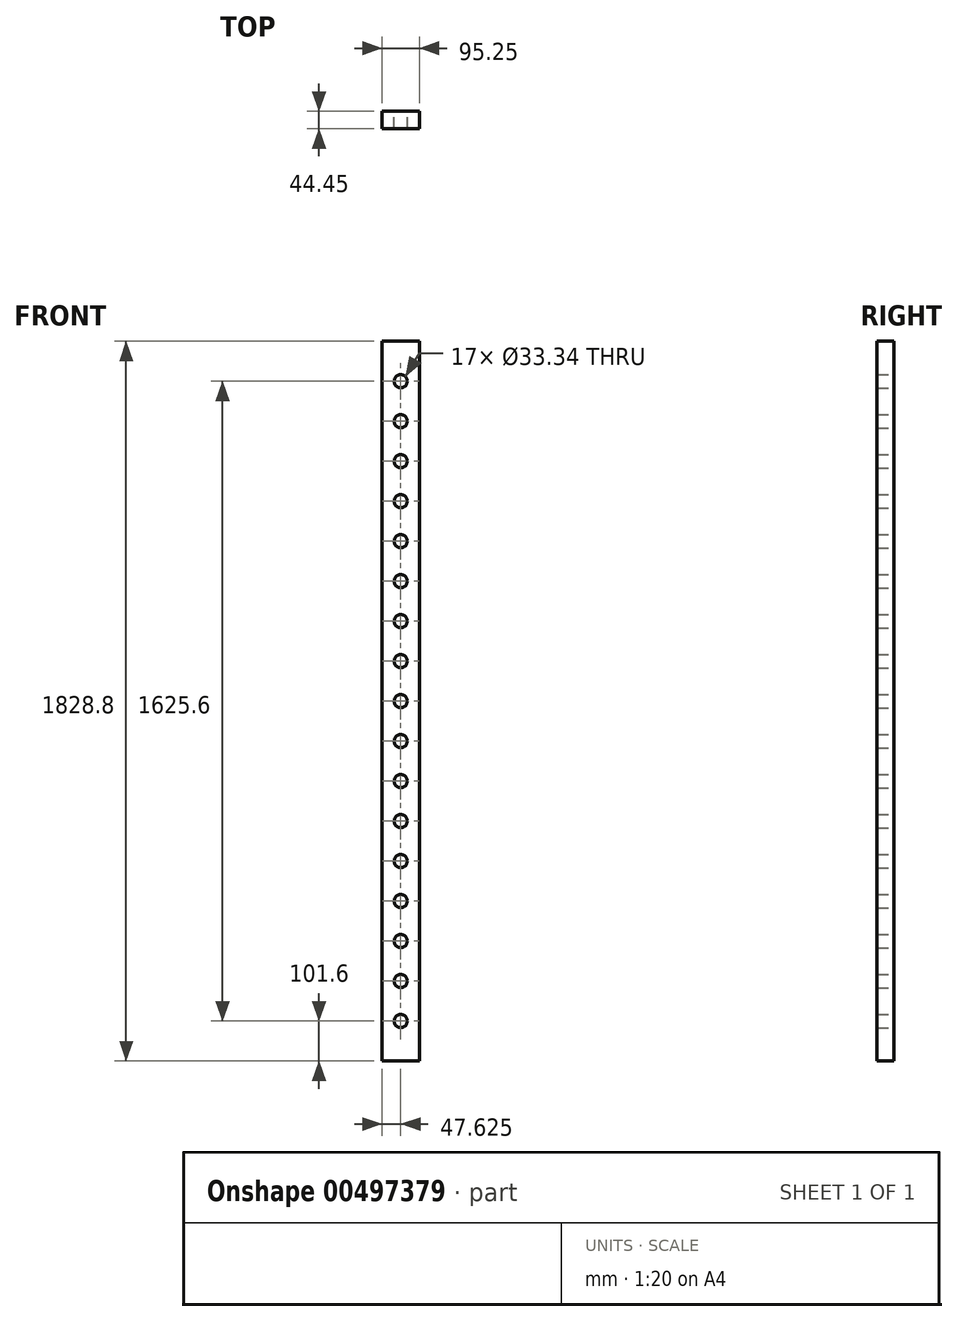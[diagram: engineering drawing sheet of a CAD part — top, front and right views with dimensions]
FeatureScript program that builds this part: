
annotation { "Feature Type Name" : "Feature", "Feature Type Description" : "" }
export const myFeature = defineFeature(function(context is Context, id is Id, definition is map)
    precondition{}
    {
        {
            var Q0;
            Q0=qCreatedBy(makeId("Front.planeOp"),FACE);
            var sketch = newSketch(context, id + "F0", { "sketchPlane" : qUnion([Q0])});
            skLineSegment(sketch, "E0.bottom", {"start": v(0, 0) * mm, "end": v(95.25, 0) * mm});
            skLineSegment(sketch, "E0.top", {"start": v(0, 1828.8) * mm, "end": v(95.25, 1828.8) * mm});
            skLineSegment(sketch, "E0.left", {"start": v(0, 0) * mm, "end": v(0, 1828.8) * mm});
            skLineSegment(sketch, "E0.right", {"start": v(95.25, 0) * mm, "end": v(95.25, 1828.8) * mm});
            skCircle(sketch, "E1", {"center": v(47.63, 101.6) * mm, "radius": 16.67 * mm});
            skCircle(sketch, "E2.0.1.0", {"center": v(47.63, 203.2) * mm, "radius": 16.67 * mm});
            skCircle(sketch, "E2.0.2.0", {"center": v(47.63, 304.8) * mm, "radius": 16.67 * mm});
            skCircle(sketch, "E2.0.3.0", {"center": v(47.63, 406.4) * mm, "radius": 16.67 * mm});
            skCircle(sketch, "E2.0.4.0", {"center": v(47.63, 508) * mm, "radius": 16.67 * mm});
            skCircle(sketch, "E2.0.5.0", {"center": v(47.63, 609.6) * mm, "radius": 16.67 * mm});
            skCircle(sketch, "E2.0.6.0", {"center": v(47.63, 711.2) * mm, "radius": 16.67 * mm});
            skCircle(sketch, "E2.0.7.0", {"center": v(47.63, 812.8) * mm, "radius": 16.67 * mm});
            skCircle(sketch, "E2.0.8.0", {"center": v(47.63, 914.4) * mm, "radius": 16.67 * mm});
            skCircle(sketch, "E2.0.9.0", {"center": v(47.63, 1016) * mm, "radius": 16.67 * mm});
            skCircle(sketch, "E2.0.10.0", {"center": v(47.63, 1117.6) * mm, "radius": 16.67 * mm});
            skCircle(sketch, "E2.0.11.0", {"center": v(47.63, 1219.2) * mm, "radius": 16.67 * mm});
            skCircle(sketch, "E2.0.12.0", {"center": v(47.63, 1320.8) * mm, "radius": 16.67 * mm});
            skCircle(sketch, "E2.0.13.0", {"center": v(47.63, 1422.4) * mm, "radius": 16.67 * mm});
            skCircle(sketch, "E2.0.14.0", {"center": v(47.63, 1524) * mm, "radius": 16.67 * mm});
            skCircle(sketch, "E2.0.15.0", {"center": v(47.63, 1625.6) * mm, "radius": 16.67 * mm});
            skCircle(sketch, "E2.0.16.0", {"center": v(47.63, 1727.2) * mm, "radius": 16.67 * mm});
            skLineSegment(sketch, "E2.direction1", {"start": v(47.63, 101.6) * mm, "end": v(73.03, 101.6) * mm, "construction": true});
            skLineSegment(sketch, "E2.direction2", {"start": v(47.63, 101.6) * mm, "end": v(47.63, 203.2) * mm, "construction": true});
            skSolve(sketch);
        }
        {
            var Q0;
            Q0 = qSketchRegion(id + "F0", true);
            extrude(context, id + "F1", {"entities" : qUnion([Q0]), "depth" : 44.45 * mm});
        }
    });
